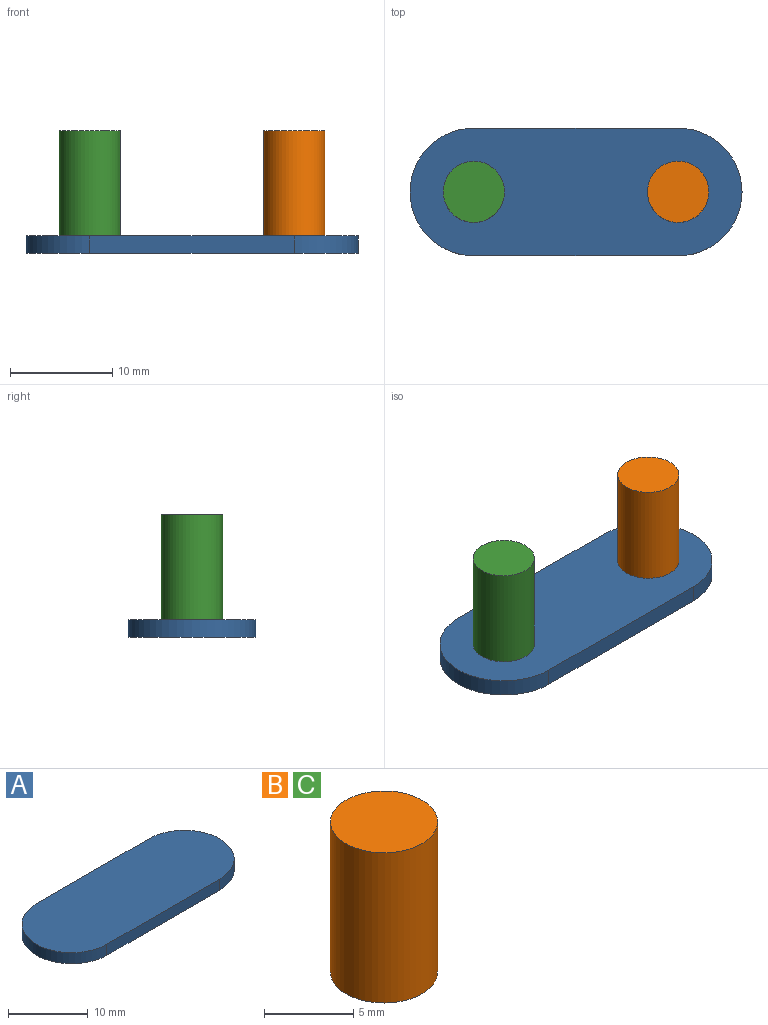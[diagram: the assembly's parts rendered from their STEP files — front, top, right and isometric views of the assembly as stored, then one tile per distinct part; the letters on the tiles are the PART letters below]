
ASSEMBLY  parts=3 mates=2
PART A: 6 faces, bbox 32.5x12.5x1.7 mm
  f0: plane 20x1.7mm, normal (0,1,0), area 34mm2, adj f1,f3,f4,f5
  f1: cylinder r=6.25mm len=12.5mm, axis (0,0,-1), area 33.4mm2, adj f0,f2,f4,f5
  f2: plane 20x1.7mm, normal (0,-1,0), area 34mm2, adj f1,f3,f4,f5
  f3: cylinder r=6.25mm len=12.5mm, axis (0,0,-1), area 33.4mm2, adj f0,f2,f4,f5
  f4: plane 32.5x12.5mm, normal (0,0,1), area 372.7mm2, adj f0,f1,f2,f3
  f5: plane 32.5x12.5mm, normal (0,0,-1), area 372.7mm2, adj f0,f1,f2,f3
PART B: 3 faces, bbox 6x6x10.3 mm
  f0: cylinder r=3mm len=10.3mm, axis (0,0,-1), area 194.2mm2, adj f1,f2
  f1: plane 6x6mm, normal (0,0,1), area 28.3mm2, adj f0
  f2: plane 6x6mm, normal (0,0,-1), area 28.3mm2, adj f0
PART C: same geometry as B
PLACE A t=(46.32,14.24,8.36)mm fixed
PLACE B t=(95.86,10.32,10.06)mm
PLACE C t=(75.86,10.32,10.06)mm
MATE fastened A.f1 <-> C.f0  axis (0,0,1) through (30.28,5.52,10.06)mm
MATE fastened A.f3 <-> B.f0  axis (0,0,1) through (50.28,5.52,10.06)mm
